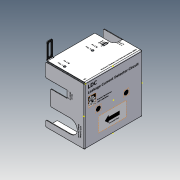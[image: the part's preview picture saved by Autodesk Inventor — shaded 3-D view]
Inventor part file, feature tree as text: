
AUTODESK INVENTOR PART (.ipt)
format: ipt  version: 2020.5 (Build 245400000, 400)  size: 730,112 bytes
history: native  units: mm
features: sketch x15, other x15, sheet_metal_op x7, projected_geometry x6, hole x1, extrude x1, chamfer x1
ambient origin geometry x8: Origin, YZ Plane, XZ Plane, XY Plane, X Axis, Y Axis, Z Axis, Center Point
bodies: Solid1 (feature_tree)
feature tree (46):
  sheet_metal_op  "Face1"
  sheet_metal_op  "Flange1"
  hole  "Hole1"  [1 undecoded]
  extrude  "Extrusion1"  Depth=1.0mm
  sheet_metal_op  "Flange4"
  chamfer  "Corner Round4"
  sketch  "Sketch24"  dims[d23=60.0mm]
  sketch  "Sketch25"  dims[d24=28.293mm]
  sketch  "Sketch26"  dims[d25=18.0mm]
  sketch  "Sketch27"  dims[d26=60.0mm d27=78.293mm d28=1.0mm d29=0.0mm d38=13.5mm d40=8.373mm d41=1.0mm d42=0.0mm d51=2.0mm d53=2.0mm d55=35.293mm d56=44.043mm d61=94.043mm d62=85.293mm d64=4.0mm d65=4.0mm d66=60.0mm d68=8.0mm d69=4.0mm d70=23.293mm d75=60.0mm d76=12.92mm d78=30.833mm d79=1.0mm d80=0.0mm d82=23.232mm d88=1.0mm d89=0.0mm d91=70.0mm d92=25.0mm d93=12.5mm d95=38.65mm d96=40.306mm d97=43.025mm d98=41.55mm d99=43.025mm d100=41.55mm d101=29.0mm d102=23.251086mm d113=27.0mm d114=3.5mm d115=6.0mm d116=4.0mm d117=2.0mm d118=90.0deg d119=1.0mm d120=20.594885mm d123=1.0mm d124=1.0mm d125=100.0mm d126=100.585786mm d127=50.0mm d128=23.0mm d130=50.0mm d140=29.0mm d148=10.0mm d149=27.560906mm d150=30.0mm d151=1.0mm d152=0.0mm d175=75.463mm d176=1.0mm d177=1.0mm d178=0.0mm d179=1.0mm d180=0.5mm d181=2.0mm d182=1.0mm d183=30.0mm d184=90.0deg d185=1.0mm d186=4.0mm d187=1.0mm d188=1.0mm d189=5.0mm d190=18.0mm d191=1.0mm d192=0.0mm d193=8.373mm d194=35.5mm d195=1.0mm d196=0.0mm d197=2.0mm d198=16.6mm d199=6.5mm d200=5.4mm d201=91.2mm d203=2.7mm d204=2.7mm d205=25.6mm d225=4.0mm d226=4.0mm d227=4.3mm d228=14.0mm d229=17.0mm d230=22.9mm d231=4.7mm d232=11.214mm d234=2.500231mm d235=14.914mm d238=20.0mm d239=2.500231mm d258=50.0mm d270=61.854839mm d271=23.0mm d272=2.2mm d273=18.0mm d283=19.287528mm d285=19.503058mm d296=2.6mm d297=9.1mm d298=2.099988mm d299=6.7mm d313=45.55mm d314=45.050107mm d322=36.050101mm d324=46.020973mm d325=2.6mm d326=9.1mm d327=2.099988mm d328=6.7mm d331=45.55mm d333=4.949893mm d334=13.949899mm d337=46.020973mm d340=8.5mm d341=2.1mm d342=2.1mm d344=7.9mm d345=44.306mm d346=23.049893mm d347=22.749893mm d348=47.406mm d349=2.1mm d350=2.0mm d351=2.0mm d352=2.1mm d353=19.999893mm d354=40.256mm d355=40.256mm d356=31.999893mm d357=6.0mm d358=6.5mm d359=2.1mm d360=2.1mm d362=26.7mm d363=38.919893mm d364=38.669893mm d365=29.8mm d366=4.3mm d367=2.1mm d368=6.0mm d369=47.292893mm d370=2.7mm d371=63.873077mm d372=6.0mm d373=47.292893mm d374=11.8mm d375=2.1mm d376=7.08mm d377=1.33mm d378=3.18mm d379=1.05mm d380=1.05mm d381=3.3mm d382=11.8mm d383=2.1mm d384=7.08mm d385=1.33mm d386=3.18mm d387=1.05mm d388=1.05mm d389=3.3mm d394=17.6mm d395=27.899893mm d396=25.82mm d397=21.92mm d398=25.7mm d399=27.604893mm d400=22.664893mm d401=17.444893mm d402=22.100107mm d403=17.6mm d404=22.395107mm d405=25.82mm d406=21.92mm d407=27.335107mm d408=25.7mm d409=32.555107mm d416=18.6mm d418=2.7mm d419=2.7mm d421=21.1mm d424=17.761013mm d425=4.351086mm d426=16.511013mm d427=8.051086mm d428=2.1mm d429=2.1mm d430=8.9mm d431=13.1mm d433=2.6mm d434=3.3mm d435=1.8mm d436=0.6mm d438=23.909893mm d439=26.009893mm d440=20.194718mm d441=23.294718mm d442=26.905472mm d443=27.908194mm d444=16.158484mm d445=26.020802mm d448=2.7mm d449=19.1mm d451=2.7mm d452=18.6mm d453=36.361013mm d454=4.351086mm d455=36.611013mm d456=8.051086mm d471=2.1mm d472=8.9mm d473=2.1mm d474=15.2mm d476=0.599999mm d477=1.799998mm d478=2.599986mm d479=3.299982mm d501=26.905472mm d502=12.841302mm d503=23.305472mm d504=11.859893mm d505=20.205472mm d506=15.009893mm d507=27.89455mm d508=24.218985mm d511=10.0mm d544=10.0mm d555=45.0mm d556=18.0mm d570=68.0mm d572=45.0mm d660=2.1mm d661=5.4mm d662=39.219893mm d663=23.6mm]
  sketch  "Sketch2"  dims[d0=102.0mm d1=102.0mm]
  other  "Plate1"
  sketch  "Sketch3"  dims[d2=1.0mm d3=1.0mm]
  other  "Plate2"
  sheet_metal_op  "Bend1"
  sheet_metal_op  "Corner1"
  sketch  "Sketch4"  dims[d4=0.5mm]
  projected_geometry  "Projected Loop1"
  sketch  "Sketch6"  dims[d5=2.0mm]
  projected_geometry  "Projected Loop3"
  sketch  "Sketch7"  dims[d6=1.0mm]
  projected_geometry  "Projected Loop4"
  sketch  "Sketch8"  dims[d7=69.4mm d8=90.0deg d9=1.0mm]
  projected_geometry  "Projected Loop5"
  sketch  "Sketch15"  dims[d10=4.0mm]
  sketch  "Sketch19"  dims[d11=1.0mm]
  projected_geometry  "Projected Loop6"
  sketch  "Sketch20"  dims[d12=1.0mm]
  other  "Plate5"
  sheet_metal_op  "Bend4"
  sheet_metal_op  "Corner4"
  sketch  "Sketch21"  dims[d13=18.0mm d14=60.0mm]
  projected_geometry  "Projected Loop7"
  sketch  "Sketch22"  dims[d22=18.0mm]
  other  "Image1"
  other  "Image2"
  other  "Image3"
  other  "Image4"
  other  "Cut1"
  other  "Cut2"
  other  "Cut3"
  other  "Cut4"
  other  "Cut8"
  other  "Cut9"
  other  "Cut10"
  other  "Definition1"
note: 1 required parameter value undecoded (feature->parameter linkage not recoverable at this tier; creation-order binding heuristic only, values carry confidence <= 0.55)
